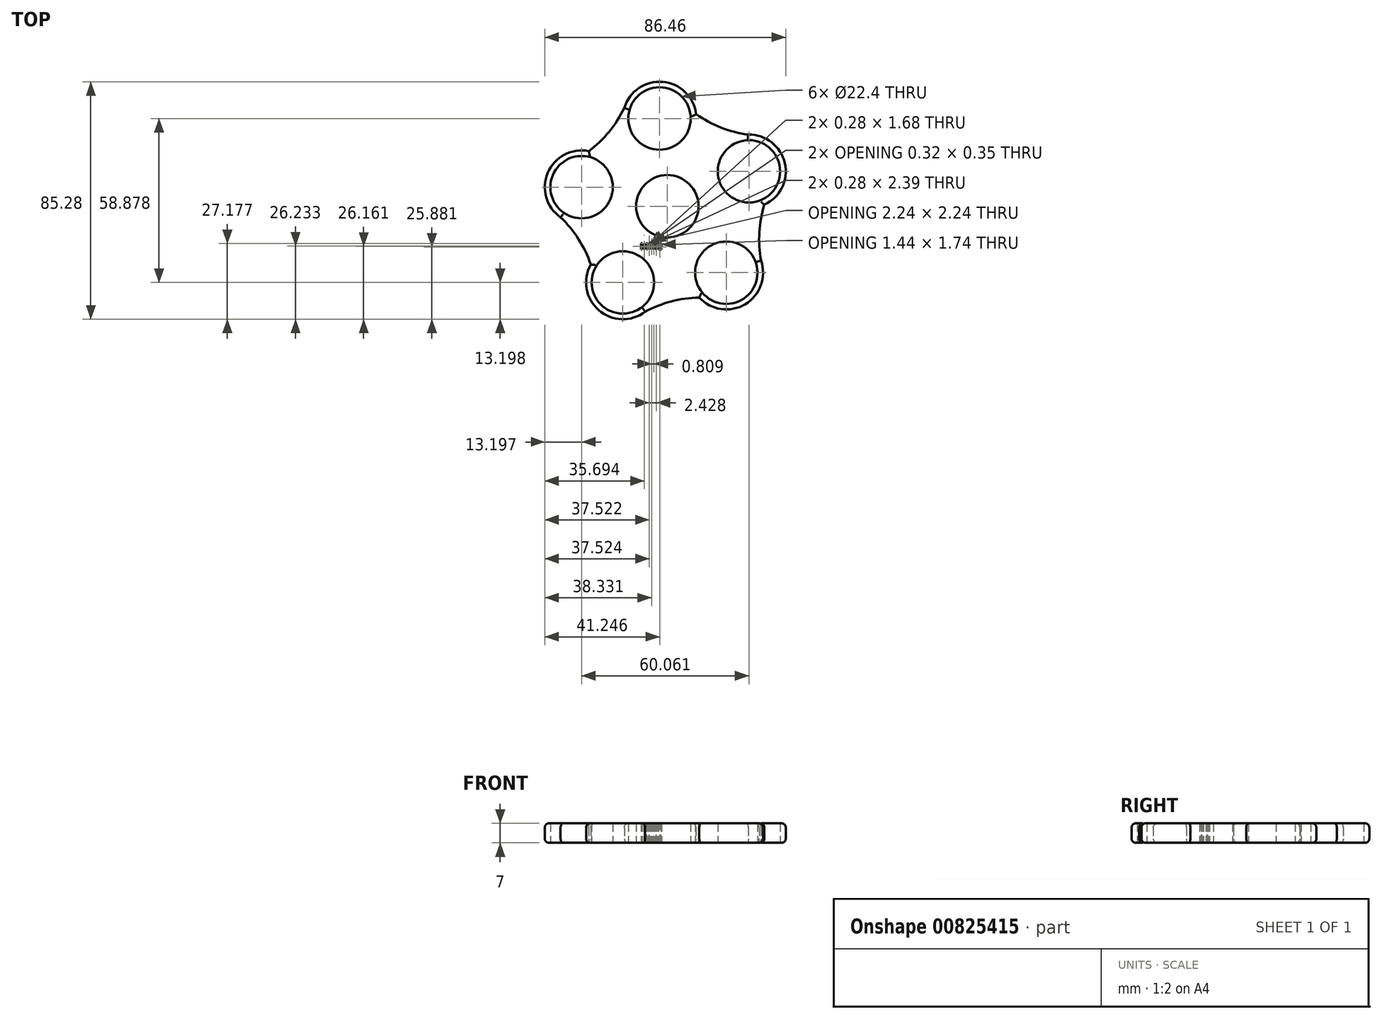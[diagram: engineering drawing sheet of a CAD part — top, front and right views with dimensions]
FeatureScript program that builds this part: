
annotation { "Feature Type Name" : "Feature", "Feature Type Description" : "" }
export const myFeature = defineFeature(function(context is Context, id is Id, definition is map)
    precondition{}
    {
        {
            var Q0;
            Q0=qCreatedBy(makeId("Top.planeOp"),FACE);
            var sketch = newSketch(context, id + "F0", { "sketchPlane" : qUnion([Q0])});
            skCircle(sketch, "E0", {"center": v(0, 0) * mm, "radius": 11.2 * mm});
            skCircle(sketch, "E1", {"center": v(-2.8, 31.52) * mm, "radius": 11.2 * mm});
            skArc(sketch, "E2", {"start": v(10.3, 33.06) * mm, "mid": v(-1.64, 44.67) * mm, "end": v(-15.44, 35.34) * mm});
            skCircle(sketch, "E3.1.0", {"center": v(-30.77, 6.86) * mm, "radius": 11.2 * mm});
            skArc(sketch, "E3.1.1", {"start": v(-28.19, 19.8) * mm, "mid": v(-42.92, 12.03) * mm, "end": v(-38.31, -3.98) * mm});
            skCircle(sketch, "E3.2.0", {"center": v(-15.96, -27.36) * mm, "radius": 11.2 * mm});
            skArc(sketch, "E3.2.1", {"start": v(-27.47, -20.9) * mm, "mid": v(-24.63, -37.31) * mm, "end": v(-7.98, -37.88) * mm});
            skCircle(sketch, "E3.3.0", {"center": v(21.16, -23.85) * mm, "radius": 11.2 * mm});
            skArc(sketch, "E3.3.1", {"start": v(11.46, -32.8) * mm, "mid": v(27.95, -35.17) * mm, "end": v(33.63, -19.51) * mm});
            skCircle(sketch, "E3.4.0", {"center": v(29.29, 12.54) * mm, "radius": 11.2 * mm});
            skArc(sketch, "E3.4.1", {"start": v(34.8, 0.55) * mm, "mid": v(42.15, 15.5) * mm, "end": v(29.02, 25.74) * mm});
            skPoint(sketch, "E3.center", {"position": v(0.18, -0.06) * mm});
            skArc(sketch, "E4", {"start": v(-28.19, 19.8) * mm, "mid": v(-19.92, 28.02) * mm, "end": v(-14.2, 38.19) * mm});
            skArc(sketch, "E5.1.0", {"start": v(-27.47, -20.9) * mm, "mid": v(-32.74, -10.5) * mm, "end": v(-40.64, -1.92) * mm});
            skArc(sketch, "E5.2.0", {"start": v(11.46, -32.8) * mm, "mid": v(-0.06, -34.6) * mm, "end": v(-10.66, -39.45) * mm});
            skArc(sketch, "E5.3.0", {"start": v(34.8, 0.55) * mm, "mid": v(32.95, -10.96) * mm, "end": v(34.3, -22.55) * mm});
            skArc(sketch, "E5.4.0", {"start": v(10.3, 33.06) * mm, "mid": v(20.68, 27.74) * mm, "end": v(32.1, 25.44) * mm});
            skText(sketch, "E6", { "text": "Millie", "fontName": "NotoSans-Regular.ttf"});
            const initialGuessF0  = {"E6": [-0.0097, -0.01552, 1, 0, 0.00226]};
            skSetInitialGuess(sketch, initialGuessF0);
            skSolve(sketch);
        }
        {
            var Q0;
            Q0 = qSketchRegion(id + "F0", true);
            extrude(context, id + "F1", {"entities" : qUnion([Q0]), "depth" : 7 * mm, "offsetDistance" : 25.4 * mm});
        }
        {
            var Q0;
            Q0=makeQuery(id+"F1.opExtrude","CAP_EDGE",EDGE,{"disambiguationData":[OSD([sQuery(id+"F0.wireOp",EDGE,"E3.2.1")])],"isStart":false});
            var Q1;
            Q1=makeQuery(id+"F1.opExtrude","CAP_EDGE",EDGE,{"disambiguationData":[OSD([sQuery(id+"F0.wireOp",EDGE,"E5.2.0")])],"isStart":false});
            var Q2;
            Q2=makeQuery(id+"F1.opExtrude","CAP_EDGE",EDGE,{"disambiguationData":[OSD([sQuery(id+"F0.wireOp",EDGE,"E5.1.0")])],"isStart":false});
            var Q3;
            Q3=makeQuery(id+"F1.opExtrude","CAP_EDGE",EDGE,{"disambiguationData":[OSD([sQuery(id+"F0.wireOp",EDGE,"E3.3.1")])],"isStart":false});
            var Q4;
            Q4=makeQuery(id+"F1.opExtrude","CAP_EDGE",EDGE,{"disambiguationData":[OSD([sQuery(id+"F0.wireOp",EDGE,"E5.3.0")])],"isStart":false});
            var Q5;
            Q5=makeQuery(id+"F1.opExtrude","CAP_EDGE",EDGE,{"disambiguationData":[OSD([sQuery(id+"F0.wireOp",EDGE,"E3.4.1")])],"isStart":false});
            var Q6;
            Q6=makeQuery(id+"F1.opExtrude","CAP_EDGE",EDGE,{"disambiguationData":[OSD([sQuery(id+"F0.wireOp",EDGE,"E5.4.0")])],"isStart":false});
            var Q7;
            Q7=makeQuery(id+"F1.opExtrude","CAP_EDGE",EDGE,{"disambiguationData":[OSD([sQuery(id+"F0.wireOp",EDGE,"E2")])],"isStart":false});
            var Q8;
            Q8=makeQuery(id+"F1.opExtrude","CAP_EDGE",EDGE,{"disambiguationData":[OSD([sQuery(id+"F0.wireOp",EDGE,"E4")])],"isStart":false});
            var Q9;
            Q9=makeQuery(id+"F1.opExtrude","CAP_EDGE",EDGE,{"disambiguationData":[OSD([sQuery(id+"F0.wireOp",EDGE,"E3.1.1")])],"isStart":false});
            fillet(context, id + "F2", {"entities" : qUnion([Q0, Q1, Q2, Q3, Q4, Q5, Q6, Q7, Q8, Q9]), "radius" : 1.5 * mm, "tangentPropagation" : true, "allowEdgeOverflow" : false});
        }
        {
            var Q0;
            Q0=makeQuery(id+"F1.opExtrude","CAP_EDGE",EDGE,{"disambiguationData":[OSD([sQuery(id+"F0.wireOp",EDGE,"E4")])],"isStart":true});
            var Q1;
            Q1=makeQuery(id+"F1.opExtrude","CAP_EDGE",EDGE,{"disambiguationData":[OSD([sQuery(id+"F0.wireOp",EDGE,"E3.1.1")])],"isStart":true});
            var Q2;
            Q2=makeQuery(id+"F1.opExtrude","CAP_EDGE",EDGE,{"disambiguationData":[OSD([sQuery(id+"F0.wireOp",EDGE,"E5.1.0")])],"isStart":true});
            var Q3;
            Q3=makeQuery(id+"F1.opExtrude","CAP_EDGE",EDGE,{"disambiguationData":[OSD([sQuery(id+"F0.wireOp",EDGE,"E3.2.1")])],"isStart":true});
            var Q4;
            Q4=makeQuery(id+"F1.opExtrude","CAP_EDGE",EDGE,{"disambiguationData":[OSD([sQuery(id+"F0.wireOp",EDGE,"E5.2.0")])],"isStart":true});
            var Q5;
            Q5=makeQuery(id+"F1.opExtrude","CAP_EDGE",EDGE,{"disambiguationData":[OSD([sQuery(id+"F0.wireOp",EDGE,"E3.3.1")])],"isStart":true});
            var Q6;
            Q6=makeQuery(id+"F1.opExtrude","CAP_EDGE",EDGE,{"disambiguationData":[OSD([sQuery(id+"F0.wireOp",EDGE,"E5.3.0")])],"isStart":true});
            var Q7;
            Q7=makeQuery(id+"F1.opExtrude","CAP_EDGE",EDGE,{"disambiguationData":[OSD([sQuery(id+"F0.wireOp",EDGE,"E3.4.1")])],"isStart":true});
            var Q8;
            Q8=makeQuery(id+"F1.opExtrude","CAP_EDGE",EDGE,{"disambiguationData":[OSD([sQuery(id+"F0.wireOp",EDGE,"E5.4.0")])],"isStart":true});
            var Q9;
            Q9=makeQuery(id+"F1.opExtrude","CAP_EDGE",EDGE,{"disambiguationData":[OSD([sQuery(id+"F0.wireOp",EDGE,"E2")])],"isStart":true});
            fillet(context, id + "F3", {"entities" : qUnion([Q0, Q1, Q2, Q3, Q4, Q5, Q6, Q7, Q8, Q9]), "radius" : 1.5 * mm, "tangentPropagation" : true, "allowEdgeOverflow" : false});
        }
    });
